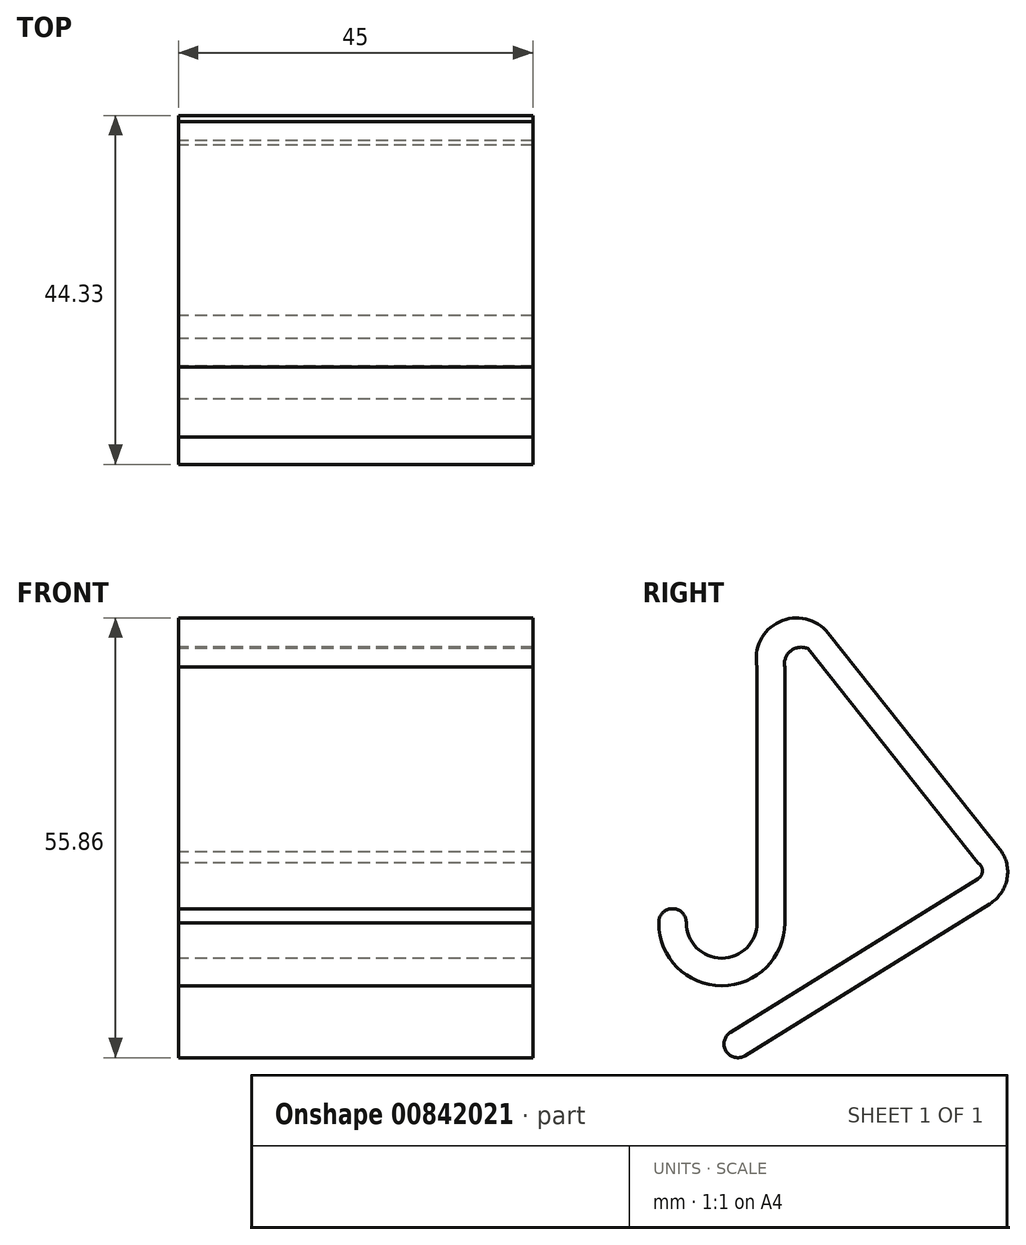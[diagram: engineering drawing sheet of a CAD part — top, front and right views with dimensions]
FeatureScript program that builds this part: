
annotation { "Feature Type Name" : "Feature", "Feature Type Description" : "" }
export const myFeature = defineFeature(function(context is Context, id is Id, definition is map)
    precondition{}
    {
        {
            var Q0;
            Q0=qCreatedBy(makeId("Right.planeOp"),FACE);
            var sketch = newSketch(context, id + "F0", { "sketchPlane" : qUnion([Q0])});
            skLineSegment(sketch, "E0", {"start": v(-23.27, 12.52) * mm, "end": v(-23.27, 45.03) * mm});
            skLineSegment(sketch, "E1", {"start": v(-19.77, 12.52) * mm, "end": v(-19.77, 45.03) * mm});
            skLineSegment(sketch, "E2", {"start": v(-16.84, 47.36) * mm, "end": v(4.8, 20.1) * mm});
            skLineSegment(sketch, "E3", {"start": v(-14.24, 49.3) * mm, "end": v(7.8, 21.55) * mm});
            skLineSegment(sketch, "E4", {"start": v(4.8, 18.11) * mm, "end": v(-26.65, -1.39) * mm});
            skLineSegment(sketch, "E5", {"start": v(-24.8, -4.36) * mm, "end": v(6.31, 14.93) * mm});
            skArc(sketch, "E6", {"start": v(-14.24, 49.3) * mm, "mid": v(-20.45, 50.75) * mm, "end": v(-23.27, 45.03) * mm});
            skArc(sketch, "E7", {"start": v(4.8, 18.11) * mm, "mid": v(5.35, 19.1) * mm, "end": v(4.8, 20.1) * mm});
            skArc(sketch, "E8", {"start": v(6.31, 14.93) * mm, "mid": v(8.44, 17.93) * mm, "end": v(7.8, 21.55) * mm});
            skArc(sketch, "E9", {"start": v(-26.65, -1.39) * mm, "mid": v(-27.21, -3.8) * mm, "end": v(-24.8, -4.36) * mm});
            skPoint(sketch, "E10.end.orphan", {"position": v(-34.26, 12.52) * mm});
            skPoint(sketch, "E10.start.orphan", {"position": v(-30.87, 12.52) * mm});
            skArc(sketch, "E11", {"start": v(-32.27, 12.52) * mm, "mid": v(-27.77, 8.02) * mm, "end": v(-23.27, 12.52) * mm});
            skArc(sketch, "E12", {"start": v(-35.77, 12.52) * mm, "mid": v(-27.77, 4.52) * mm, "end": v(-19.77, 12.52) * mm});
            skArc(sketch, "E13", {"start": v(-32.27, 12.52) * mm, "mid": v(-34.02, 14.3) * mm, "end": v(-35.77, 12.52) * mm});
            skArc(sketch, "E14", {"start": v(-16.84, 47.36) * mm, "mid": v(-19, 47.06) * mm, "end": v(-19.77, 45.03) * mm});
            skSolve(sketch);
        }
        {
            var Q0;
            Q0 = qSketchRegion(id + "F0", true);
            extrude(context, id + "F1", {"entities" : qUnion([Q0]), "depth" : 45 * mm, "offsetDistance" : 25 * mm});
        }
    });
